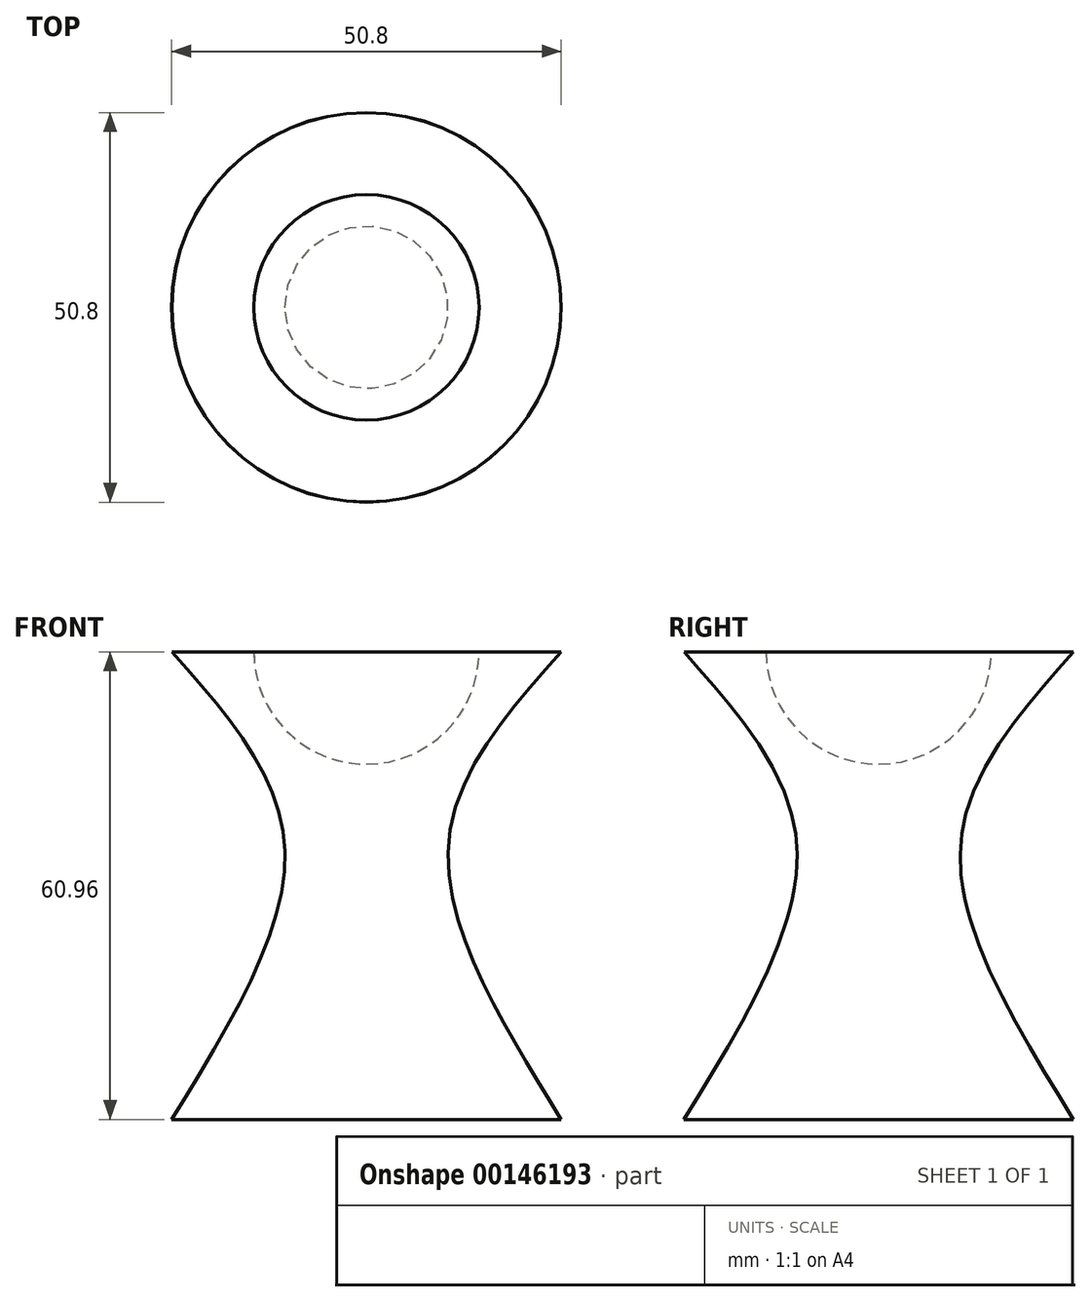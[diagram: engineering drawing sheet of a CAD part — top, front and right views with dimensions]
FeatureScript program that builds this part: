
annotation { "Feature Type Name" : "Feature", "Feature Type Description" : "" }
export const myFeature = defineFeature(function(context is Context, id is Id, definition is map)
    precondition{}
    {
        {
            var Q0;
            Q0=qCreatedBy(makeId("Top.planeOp"),FACE);
            var sketch = newSketch(context, id + "F0", { "sketchPlane" : qUnion([Q0])});
            skCircle(sketch, "E0", {"center": v(0, 0) * mm, "radius": 25.4 * mm});
            skSolve(sketch);
        }
        {
            var Q0;
            Q0 = qSketchRegion(id + "F0", true);
            extrude(context, id + "F1", {"entities" : qUnion([Q0]), "depth" : 60.96 * mm});
        }
        {
            var Q0;
            Q0=qCreatedBy(makeId("Front.planeOp"),FACE);
            var sketch = newSketch(context, id + "F2", { "sketchPlane" : qUnion([Q0])});
            skLineSegment(sketch, "E1", {"start": v(0, 69.83) * mm, "end": v(0, -34.98) * mm, "construction": true});
            skLineSegment(sketch, "E2", {"start": v(-25.4, 70.58) * mm, "end": v(-25.4, -35.16) * mm, "construction": true});
            skLineSegment(sketch, "E3", {"start": v(-67.92, 50.4) * mm, "end": v(-67.92, -49.73) * mm, "construction": true});
            skLineSegment(sketch, "E4", {"start": v(-32.48, 60.98) * mm, "end": v(44.84, 60.98) * mm, "construction": true});
            skFitSpline(sketch, "E5", {"points": [v(-25.4, 60.98) * mm, v(-10.67, 35.77) * mm, v(-25.4, 0) * mm], "startDerivative": vector(45.44, -51.3) * mm, "endDerivative": vector(-43.36, -70.23) * mm});
            skLineSegment(sketch, "E6", {"start": v(-25.4, 60.98) * mm, "end": v(-25.4, 0) * mm});
            skSolve(sketch);
        }
        {
            var Q0;
            Q0 = qSketchRegion(id + "F2", true);
            var Q1;
            Q1=sQuery(id+"F2.wireOp",EDGE,"E1");
            revolve(context, id + "F3", {"operationType" : NewBodyOperationType.REMOVE, "entities" : qUnion([Q0]), "axis" : qUnion([Q1]), "revolveType" : RevolveType.FULL, "oppositeDirection" : true});
        }
        {
            var Q0;
            Q0=qCreatedBy(makeId("Front.planeOp"),FACE);
            var sketch = newSketch(context, id + "F4", { "sketchPlane" : qUnion([Q0])});
            skArc(sketch, "E7", {"start": v(0, 46.31) * mm, "mid": v(14.69, 61) * mm, "end": v(0, 75.7) * mm});
            skLineSegment(sketch, "E8", {"start": v(0, 75.7) * mm, "end": v(0, 46.31) * mm});
            skSolve(sketch);
        }
        {
            var Q0;
            Q0 = qSketchRegion(id + "F4", true);
            var Q1;
            Q1=sQuery(id+"F4.wireOp",EDGE,"E8");
            revolve(context, id + "F5", {"operationType" : NewBodyOperationType.REMOVE, "entities" : qUnion([Q0]), "axis" : qUnion([Q1]), "revolveType" : RevolveType.FULL, "oppositeDirection" : true});
        }
    });
